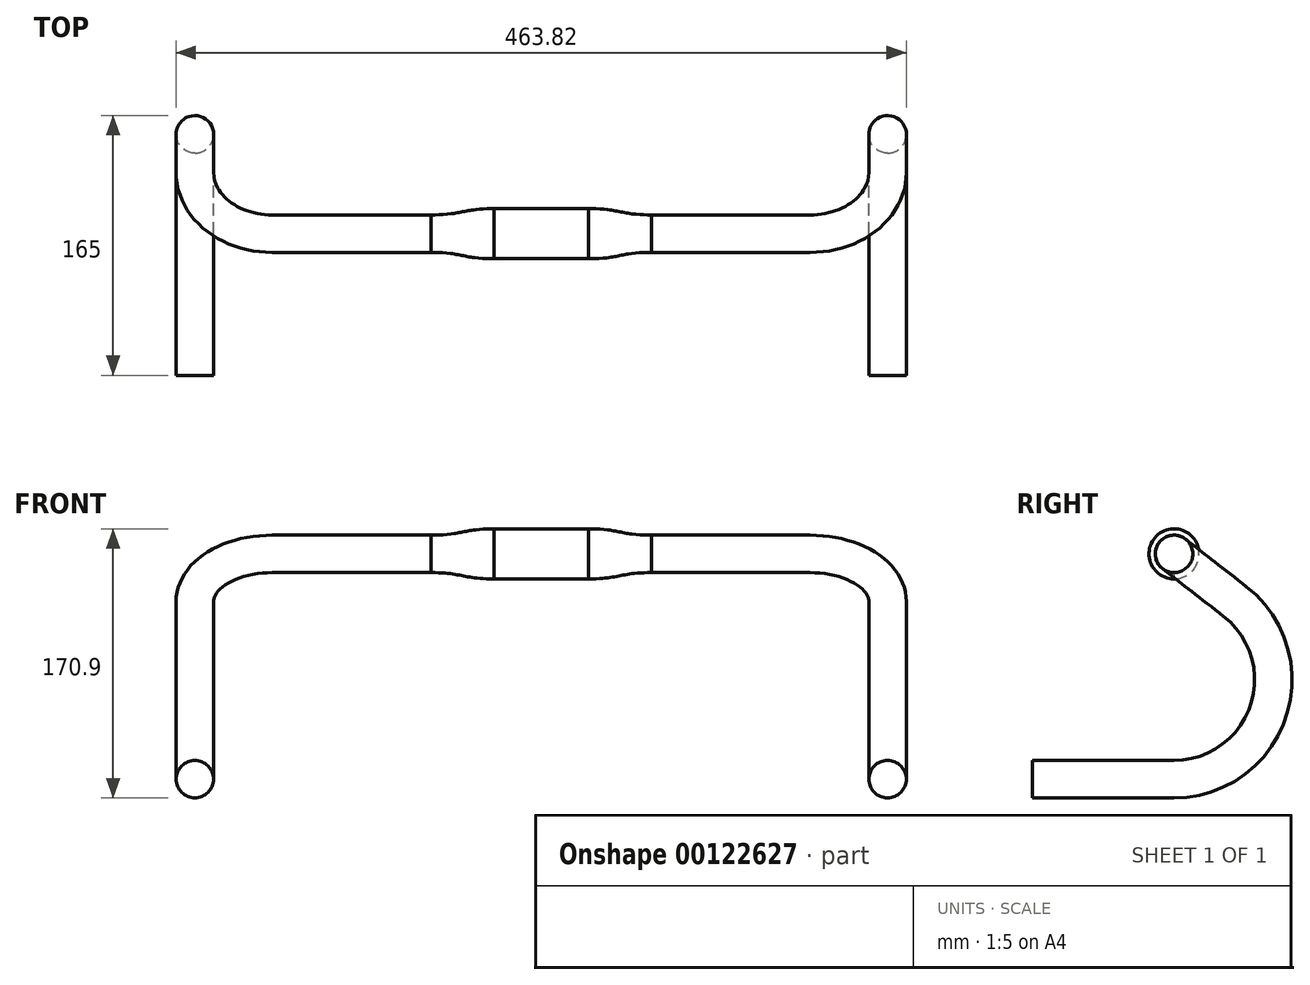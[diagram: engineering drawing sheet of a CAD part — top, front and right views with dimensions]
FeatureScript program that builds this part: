
annotation { "Feature Type Name" : "Feature", "Feature Type Description" : "" }
export const myFeature = defineFeature(function(context is Context, id is Id, definition is map)
    precondition{}
    {
        {
            var Q0;
            Q0=qCreatedBy(makeId("Right.planeOp"),FACE);
            var sketch = newSketch(context, id + "F0", { "sketchPlane" : qUnion([Q0])});
            skCircle(sketch, "E0", {"center": v(0, 0) * mm, "radius": 15.9 * mm});
            skLineSegment(sketch, "E1", {"start": v(75, 0) * mm, "end": v(75, -155) * mm, "construction": true});
            skLineSegment(sketch, "E2", {"start": v(75, -155) * mm, "end": v(-90, -155) * mm, "construction": true});
            skSolve(sketch);
        }
        {
            var Q0;
            Q0=qCreatedBy(makeId("Top.planeOp"),FACE);
            var Q1;
            Q1=sQuery(id+"F0.wireOp",VERTEX,"E2.end");
            cPlane(context, id + "F1", {"entities" : qUnion([Q0, Q1]), "cplaneType" : CPlaneType.PLANE_POINT, "offset" : 25 * mm, "width" : 150 * mm, "height" : 150 * mm});
        }
        {
            var Q0;
            Q0=qCreatedBy(id+"F1.planeOp",FACE);
            var sketch = newSketch(context, id + "F2", { "sketchPlane" : qUnion([Q0])});
            skPoint(sketch, "E3", {"position": v(220, -90) * mm});
            skPoint(sketch, "E4.MirrorP", {"position": v(-220, -90) * mm});
            skLineSegment(sketch, "E5", {"start": v(220, -90) * mm, "end": v(220, 0) * mm, "construction": true});
            skSolve(sketch);
        }
        {
            var Q0;
            Q0=sQuery(id+"F2.wireOp",VERTEX,"E3");
            var Q1;
            Q1=sQuery(id+"F2.wireOp",EDGE,"E5");
            cPlane(context, id + "F3", {"entities" : qUnion([Q0, Q1]), "cplaneType" : CPlaneType.LINE_POINT, "offset" : 25 * mm, "width" : 150 * mm, "height" : 150 * mm});
        }
        {
            var Q0;
            Q0=qCreatedBy(id+"F3.planeOp",FACE);
            var sketch = newSketch(context, id + "F4", { "sketchPlane" : qUnion([Q0])});
            skPoint(sketch, "E6.0", {"position": v(-220, -155) * mm});
            skCircle(sketch, "E7", {"center": v(-220, -143.1) * mm, "radius": 11.9 * mm});
            skLineSegment(sketch, "E8", {"start": v(-220, -143.1) * mm, "end": v(-220, 0) * mm, "construction": true});
            skSolve(sketch);
        }
        {
            var Q0;
            Q0=sQuery(id+"F4.wireOp",EDGE,"E8");
            var Q1;
            Q1=sQuery(id+"F2.wireOp",EDGE,"E5");
            cPlane(context, id + "F5", {"entities" : qUnion([Q0, Q1]), "cplaneType" : CPlaneType.LINE_ANGLE, "offset" : 25 * mm, "angle" : 0 * degree, "width" : 150 * mm, "height" : 150 * mm});
        }
        {
            var Q0;
            Q0=qCreatedBy(makeId("Front.planeOp"),FACE);
            var sketch = newSketch(context, id + "F6", { "sketchPlane" : qUnion([Q0])});
            skLineSegment(sketch, "E9", {"start": v(0, 0) * mm, "end": v(274.67, 0) * mm, "construction": true});
            skSolve(sketch);
        }
        {
            var Q0;
            Q0=sQuery(id+"F0.wireOp",EDGE,"E1");
            var Q1;
            Q1=qCreatedBy(makeId("Front.planeOp"),FACE);
            cPlane(context, id + "F7", {"entities" : qUnion([Q0, Q1]), "cplaneType" : CPlaneType.LINE_ANGLE, "offset" : 25 * mm, "angle" : 0 * degree, "width" : 150 * mm, "height" : 150 * mm});
        }
        {
            var Q0;
            Q0=qCreatedBy(id+"F5.planeOp",FACE);
            var sketch = newSketch(context, id + "F8", { "sketchPlane" : qUnion([Q0])});
            skLineSegment(sketch, "E10", {"start": v(-75, -155) * mm, "end": v(-75, 0) * mm, "construction": true});
            skPoint(sketch, "E11", {"position": v(90, -155) * mm});
            skLineSegment(sketch, "E12", {"start": v(90, -155) * mm, "end": v(0, -155) * mm, "construction": true});
            skArc(sketch, "E13", {"start": v(-46.11, -20.85) * mm, "mid": v(-70.93, -104.38) * mm, "end": v(0, -155) * mm, "construction": true});
            skLineSegment(sketch, "E14", {"start": v(0, -80) * mm, "end": v(0, -155) * mm, "construction": true});
            skPoint(sketch, "E15.0", {"position": v(90, -143.1) * mm});
            skLineSegment(sketch, "E16", {"start": v(90, -143.1) * mm, "end": v(0, -143.1) * mm});
            skLineSegment(sketch, "E17", {"start": v(-38.8, -30.24) * mm, "end": v(-38.8, -30.24) * mm});
            skLineSegment(sketch, "E18", {"start": v(0, -80) * mm, "end": v(-38.8, -30.24) * mm, "construction": true});
            skArc(sketch, "E19", {"start": v(-38.8, -30.24) * mm, "mid": v(-59.67, -100.5) * mm, "end": v(0, -143.1) * mm});
            skLineSegment(sketch, "E20", {"start": v(-38.8, -30.24) * mm, "end": v(0, 0) * mm, "construction": true});
            skPoint(sketch, "E21", {"position": v(0, 0) * mm});
            skSolve(sketch);
        }
        {
            var Q0;
            Q0=sQuery(id+"F8.wireOp",VERTEX,"E19.start");
            var Q1;
            Q1=sQuery(id+"F8.wireOp",VERTEX,"E20.end");
            var Q2;
            Q2=sQuery(id+"F0.wireOp",VERTEX,"E0.center");
            cPlane(context, id + "F9", {"entities" : qUnion([Q0, Q1, Q2]), "cplaneType" : CPlaneType.THREE_POINT, "offset" : 25 * mm, "width" : 150 * mm, "height" : 150 * mm});
        }
        {
            var Q0;
            Q0=qCreatedBy(id+"F9.planeOp",FACE);
            var sketch = newSketch(context, id + "F10", { "sketchPlane" : qUnion([Q0])});
            skLineSegment(sketch, "E22", {"start": v(220, 0) * mm, "end": v(170.81, 0) * mm, "construction": true});
            skLineSegment(sketch, "E23", {"start": v(170.81, 0) * mm, "end": v(0, 0) * mm});
            skArc(sketch, "E24", {"start": v(170.81, 0) * mm, "mid": v(205.6, 14.4) * mm, "end": v(220, 49.19) * mm});
            skSolve(sketch);
        }
        {
            var Q0;
            Q0=makeQuery(id+"F4.imprint","IMPRINT",FACE,{"disambiguationData":[TD([[makeQuery(id+"F4.imprint","IMPRINT",EDGE,{"derivedFrom":sQuery(id+"F4.wireOp",EDGE,"E7")}),1.0]])]});
            var Q1;
            Q1=sQuery(id+"F8.wireOp",EDGE,"E16");
            var Q2;
            Q2=sQuery(id+"F8.wireOp",EDGE,"E19");
            var Q3;
            Q3=sQuery(id+"F10.wireOp",EDGE,"E24");
            sweep(context, id + "F11", {"profiles" : qUnion([Q0]), "path" : qUnion([Q1, Q2, Q3])});
        }
        {
            var Q0;
            Q0=qCreatedBy(id+"F9.planeOp",FACE);
            var sketch = newSketch(context, id + "F12", { "sketchPlane" : qUnion([Q0])});
            skPoint(sketch, "E25", {"position": v(170.81, -11.9) * mm});
            skPoint(sketch, "E26", {"position": v(0, -15.9) * mm});
            skLineSegment(sketch, "E27", {"start": v(170.81, -11.9) * mm, "end": v(70, -11.9) * mm, "construction": true});
            skLineSegment(sketch, "E28", {"start": v(0, -15.9) * mm, "end": v(30, -15.9) * mm});
            skFitSpline(sketch, "E29", {"points": [v(70, -11.9) * mm, v(30, -15.9) * mm], "startDerivative": vector(-60, 0) * mm, "endDerivative": vector(-60, 0) * mm});
            skLineSegment(sketch, "E30", {"start": v(50, -11.9) * mm, "end": v(70, -11.9) * mm, "construction": true});
            skLineSegment(sketch, "E31", {"start": v(30, -15.9) * mm, "end": v(50, -15.9) * mm, "construction": true});
            skLineSegment(sketch, "E32.0", {"start": v(170.81, 0) * mm, "end": v(70, 0) * mm, "construction": true});
            skLineSegment(sketch, "E33", {"start": v(170.81, -11.9) * mm, "end": v(170.81, 0) * mm, "construction": true});
            skLineSegment(sketch, "E34", {"start": v(0, -15.9) * mm, "end": v(0, 0) * mm});
            skLineSegment(sketch, "E35", {"start": v(70, -11.9) * mm, "end": v(70, 0) * mm});
            skLineSegment(sketch, "E36", {"start": v(70, 0) * mm, "end": v(0, 0) * mm});
            skSolve(sketch);
        }
        {
            var Q0;
            Q0=makeQuery(id+"F12.imprint","IMPRINT",FACE,{"disambiguationData":[TD([[makeQuery(id+"F12.imprint","IMPRINT",EDGE,{"derivedFrom":sQuery(id+"F12.wireOp",EDGE,"E28")}),1.0]])]});
            var Q1;
            Q1=sQuery(id+"F10.wireOp",EDGE,"E23");
            revolve(context, id + "F13", {"entities" : qUnion([Q0]), "axis" : qUnion([Q1]), "revolveType" : RevolveType.FULL});
        }
        {
            var Q2;
            Q2=makeQuery(id+"F11.opSweep","CAP_FACE",FACE,{"disambiguationData":[OSD([sQuery(id+"F4.wireOp",EDGE,"E7"),sQuery(id+"F10.wireOp",VERTEX,"E24.start")])],"isStart":false});
            var Q3;
            Q3=makeQuery(id+"F13.opRevolve","SWEPT_FACE",FACE,{"disambiguationData":[OSD([sQuery(id+"F12.wireOp",EDGE,"E35")])]});
            loft(context, id + "F14", {"operationType" : NewBodyOperationType.ADD, "sheetProfilesArray" : [{ "sheetProfileEntities" : qUnion([Q2]) }, { "sheetProfileEntities" : qUnion([Q3]) }]});
        }
        {
            var Q0;
            Q0=makeQuery(id+"F11.opSweep","SWEPT_BODY",BODY,{"disambiguationData":[OSD([sQuery(id+"F4.wireOp",EDGE,"E7"),sQuery(id+"F10.wireOp",EDGE,"E24")])]});
            var Q1;
            Q1=qCreatedBy(makeId("Right.planeOp"),FACE);
            mirror(context, id + "F15", {"operationType" : NewBodyOperationType.ADD, "entities" : qUnion([Q0]), "mirrorPlane" : qUnion([Q1])});
        }
    });
